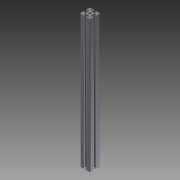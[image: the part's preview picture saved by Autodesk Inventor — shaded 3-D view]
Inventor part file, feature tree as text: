
AUTODESK INVENTOR PART (.ipt)
format: ipt  version: 2016 (Build 200138000, 138)  size: 215,040 bytes
history: native  units: mm
features: other x42, sketch x5, hole x4, extrude x1
ambient origin geometry x8: Origin, YZ Plane, XZ Plane, XY Plane, X Axis, Y Axis, Z Axis, Center Point
bodies: Solid1 (feature_tree)
feature tree (52):
  extrude  "Extrusion1"  [1 undecoded]
  hole  "Drilling 1"  [1 undecoded]
  hole  "Drilling 2"  [1 undecoded]
  hole  "Drilling 3"  [1 undecoded]
  hole  "Drilling 4"  [1 undecoded]
  other  "side_4d_XY"
  other  "side_4d_YZ"
  other  "side_4d_ZX"
  other  "side_4d_X"
  other  "side_4d_Y"
  other  "side_4d_Z"
  other  "side_4d_Center"
  other  "side_1a_XY"
  other  "side_1a_YZ"
  other  "side_1a_ZX"
  other  "side_1a_X"
  other  "side_1a_Y"
  other  "side_1a_Z"
  other  "side_1a_Center"
  other  "side_2b_XY"
  other  "side_2b_YZ"
  other  "side_2b_ZX"
  other  "side_2b_X"
  other  "side_2b_Y"
  other  "side_2b_Z"
  other  "side_2b_Center"
  other  "side_3c_XY"
  other  "side_3c_YZ"
  other  "side_3c_ZX"
  other  "side_3c_X"
  other  "side_3c_Y"
  other  "side_3c_Z"
  other  "side_3c_Center"
  other  "end_XY"
  other  "end_YZ"
  other  "end_ZX"
  other  "end_X"
  other  "end_Y"
  other  "end_Z"
  other  "end_Center"
  other  "start_XY"
  other  "start_YZ"
  other  "start_ZX"
  other  "start_X"
  other  "start_Y"
  other  "start_Z"
  other  "start_Center"
  sketch  "Skizze_1"  dims[d0=545.0mm d1=0.0mm]
  sketch  "Sketch2"  dims[d2=5.0mm d3=6.0mm d4=4.0mm d5=2.0mm d6=90.0deg d7=6000.0mm d8=0.0mm]
  sketch  "Sketch3"  dims[d9=5.0mm d10=6.0mm d11=4.0mm d12=2.0mm d13=90.0deg d14=6000.0mm d15=0.0mm]
  sketch  "Sketch4"  dims[d16=5.0mm d17=6.0mm d18=4.0mm d19=2.0mm d20=90.0deg d21=6000.0mm d22=0.0mm]
  sketch  "Sketch5"  dims[d23=5.0mm d24=6.0mm d25=4.0mm d26=2.0mm d27=90.0deg d28=6000.0mm d29=0.0mm]
note: 5 required parameter values undecoded (feature->parameter linkage not recoverable at this tier; creation-order binding heuristic only, values carry confidence <= 0.55)
